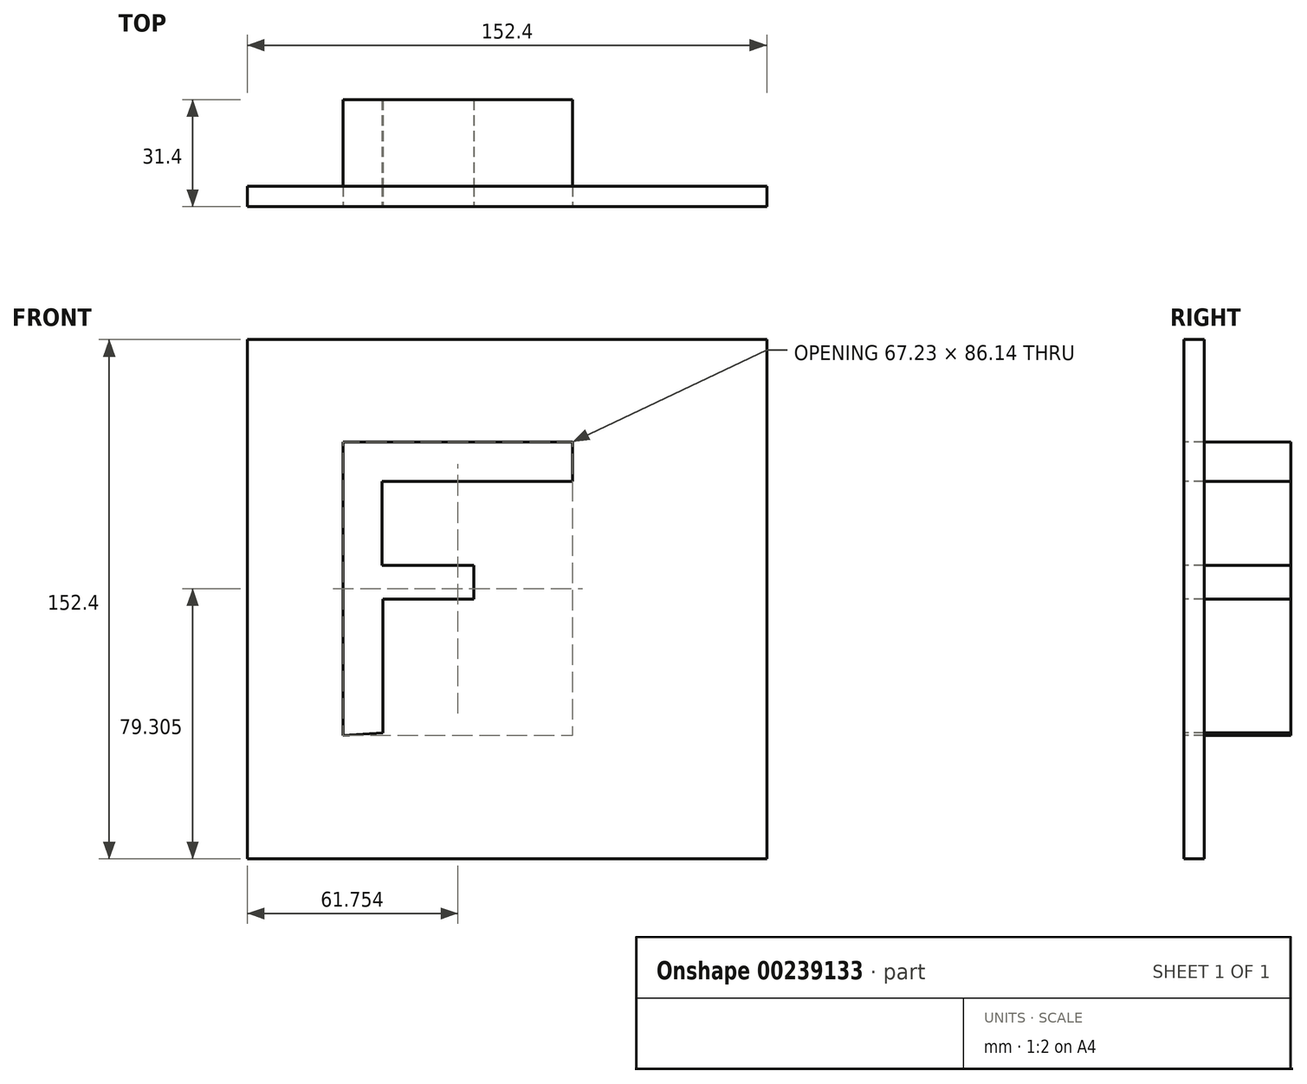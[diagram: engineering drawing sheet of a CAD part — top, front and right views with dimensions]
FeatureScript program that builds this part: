
annotation { "Feature Type Name" : "Feature", "Feature Type Description" : "" }
export const myFeature = defineFeature(function(context is Context, id is Id, definition is map)
    precondition{}
    {
        {
            assignVariable(context, id + "F0", {"name" : "L", "anyValue" : 6});
        }
        {
            var Q0;
            Q0=qCreatedBy(makeId("Front.planeOp"),FACE);
            var sketch = newSketch(context, id + "F1", { "sketchPlane" : qUnion([Q0])});
            skLineSegment(sketch, "E0.bottom", {"start": v(-76.2, 76.2) * mm, "end": v(76.2, 76.2) * mm});
            skLineSegment(sketch, "E0.top", {"start": v(-76.2, -76.2) * mm, "end": v(76.2, -76.2) * mm});
            skLineSegment(sketch, "E0.left", {"start": v(-76.2, 76.2) * mm, "end": v(-76.2, -76.2) * mm});
            skLineSegment(sketch, "E0.right", {"start": v(76.2, 76.2) * mm, "end": v(76.2, -76.2) * mm});
            skPoint(sketch, "E0.middle", {"position": v(0, 0) * mm});
            skSolve(sketch);
        }
        {
            var Q0;
            Q0=makeQuery(id+"F1.imprint","IMPRINT",FACE,{"disambiguationData":[TD([[makeQuery(id+"F1.imprint","IMPRINT",EDGE,{"derivedFrom":sQuery(id+"F1.wireOp",EDGE,"E0.bottom")}),-1.0]])]});
            extrude(context, id + "F2", {"entities" : qUnion([Q0]), "endBound" : BoundingType.SYMMETRIC, "depth" : (getVariable(context, 'L')) * mm});
        }
        {
            var Q0;
            Q0=makeQuery(id+"F2.opExtrude","CAP_FACE",FACE,{"disambiguationData":[OSD([sQuery(id+"F1.wireOp",EDGE,"E0.bottom"),sQuery(id+"F1.wireOp",EDGE,"E0.top"),sQuery(id+"F1.wireOp",EDGE,"E0.left"),sQuery(id+"F1.wireOp",EDGE,"E0.right")])],"isStart":false});
            var sketch = newSketch(context, id + "F3", { "sketchPlane" : qUnion([Q0])});
            skLineSegment(sketch, "E1", {"start": v(-48.06, 46.17) * mm, "end": v(-48.06, -39.96) * mm});
            skLineSegment(sketch, "E2", {"start": v(-48.06, 46.17) * mm, "end": v(19.17, 46.17) * mm});
            skLineSegment(sketch, "E3", {"start": v(19.17, 46.17) * mm, "end": v(19.17, 34.56) * mm});
            skLineSegment(sketch, "E4", {"start": v(19.17, 34.56) * mm, "end": v(-36.72, 34.56) * mm});
            skLineSegment(sketch, "E5", {"start": v(-36.72, 34.56) * mm, "end": v(-36.72, 10) * mm});
            skLineSegment(sketch, "E6", {"start": v(-36.72, 10) * mm, "end": v(-9.72, 10) * mm});
            skLineSegment(sketch, "E7", {"start": v(-9.72, 10) * mm, "end": v(-9.72, 0) * mm});
            skLineSegment(sketch, "E8", {"start": v(-9.72, 0) * mm, "end": v(-36.45, 0) * mm});
            skLineSegment(sketch, "E9", {"start": v(-36.45, 0) * mm, "end": v(-36.45, -39.15) * mm});
            skLineSegment(sketch, "E10", {"start": v(-36.45, -39.15) * mm, "end": v(-48.06, -39.96) * mm});
            skSolve(sketch);
        }
        {
            var Q0;
            Q0=makeQuery(id+"F3.imprint","IMPRINT",FACE,{"disambiguationData":[TD([[makeQuery(id+"F3.imprint","IMPRINT",EDGE,{"derivedFrom":sQuery(id+"F3.wireOp",EDGE,"E1")}),1.0]])]});
            extrude(context, id + "F4", {"entities" : qUnion([Q0]), "operationType" : NewBodyOperationType.REMOVE, "oppositeDirection" : true, "depth" : 25.4 * mm});
        }
        {
            var Q0;
            Q0=makeQuery(id+"F2.opExtrude","CAP_FACE",FACE,{"disambiguationData":[OSD([sQuery(id+"F1.wireOp",EDGE,"E0.bottom"),sQuery(id+"F1.wireOp",EDGE,"E0.top"),sQuery(id+"F1.wireOp",EDGE,"E0.left"),sQuery(id+"F1.wireOp",EDGE,"E0.right")])],"isStart":true});
            var sketch = newSketch(context, id + "F5", { "sketchPlane" : qUnion([Q0])});
            skPoint(sketch, "E11.0", {"position": v(-19.17, 46.17) * mm});
            skPoint(sketch, "E12.0", {"position": v(-19.17, 34.56) * mm});
            skPoint(sketch, "E13.0", {"position": v(36.72, 34.56) * mm});
            skPoint(sketch, "E14.0", {"position": v(36.72, 10) * mm});
            skPoint(sketch, "E15.0", {"position": v(9.72, 10) * mm});
            skPoint(sketch, "E16.0", {"position": v(9.72, 0) * mm});
            skPoint(sketch, "E17.0", {"position": v(36.45, 0) * mm});
            skPoint(sketch, "E18.0", {"position": v(36.45, -39.15) * mm});
            skPoint(sketch, "E19.0", {"position": v(48.06, -39.96) * mm});
            skPoint(sketch, "E20.0", {"position": v(48.06, 46.17) * mm});
            skLineSegment(sketch, "E21.0", {"start": v(48.06, 46.17) * mm, "end": v(-19.17, 46.17) * mm});
            skLineSegment(sketch, "E22.0", {"start": v(-19.17, 46.17) * mm, "end": v(-19.17, 34.56) * mm});
            skLineSegment(sketch, "E23.0", {"start": v(36.72, 34.56) * mm, "end": v(36.72, 10) * mm});
            skPoint(sketch, "E24.0", {"position": v(8.78, 34.56) * mm});
            skLineSegment(sketch, "E25.0", {"start": v(-19.17, 34.56) * mm, "end": v(36.72, 34.56) * mm});
            skPoint(sketch, "E26.0", {"position": v(23.22, 10) * mm});
            skLineSegment(sketch, "E27.0", {"start": v(36.72, 10) * mm, "end": v(9.72, 10) * mm});
            skLineSegment(sketch, "E28.0", {"start": v(9.72, 10) * mm, "end": v(9.72, 0) * mm});
            skLineSegment(sketch, "E29.0", {"start": v(9.72, 0) * mm, "end": v(36.45, 0) * mm});
            skLineSegment(sketch, "E30.0", {"start": v(36.45, 0) * mm, "end": v(36.45, -39.15) * mm});
            skPoint(sketch, "E31.0", {"position": v(42.26, -39.56) * mm});
            skLineSegment(sketch, "E32.0", {"start": v(48.06, 46.17) * mm, "end": v(48.06, -39.96) * mm});
            skLineSegment(sketch, "E33.0", {"start": v(36.45, -39.15) * mm, "end": v(48.06, -39.96) * mm});
            skSolve(sketch);
        }
        {
            var Q0;
            Q0=makeQuery(id+"F5.imprint","IMPRINT",FACE,{"disambiguationData":[TD([[makeQuery(id+"F5.imprint","IMPRINT",EDGE,{"derivedFrom":sQuery(id+"F5.wireOp",EDGE,"E21.0")}),1.0]])]});
            extrude(context, id + "F6", {"entities" : qUnion([Q0]), "operationType" : NewBodyOperationType.ADD, "depth" : 25.4 * mm});
        }
    });
